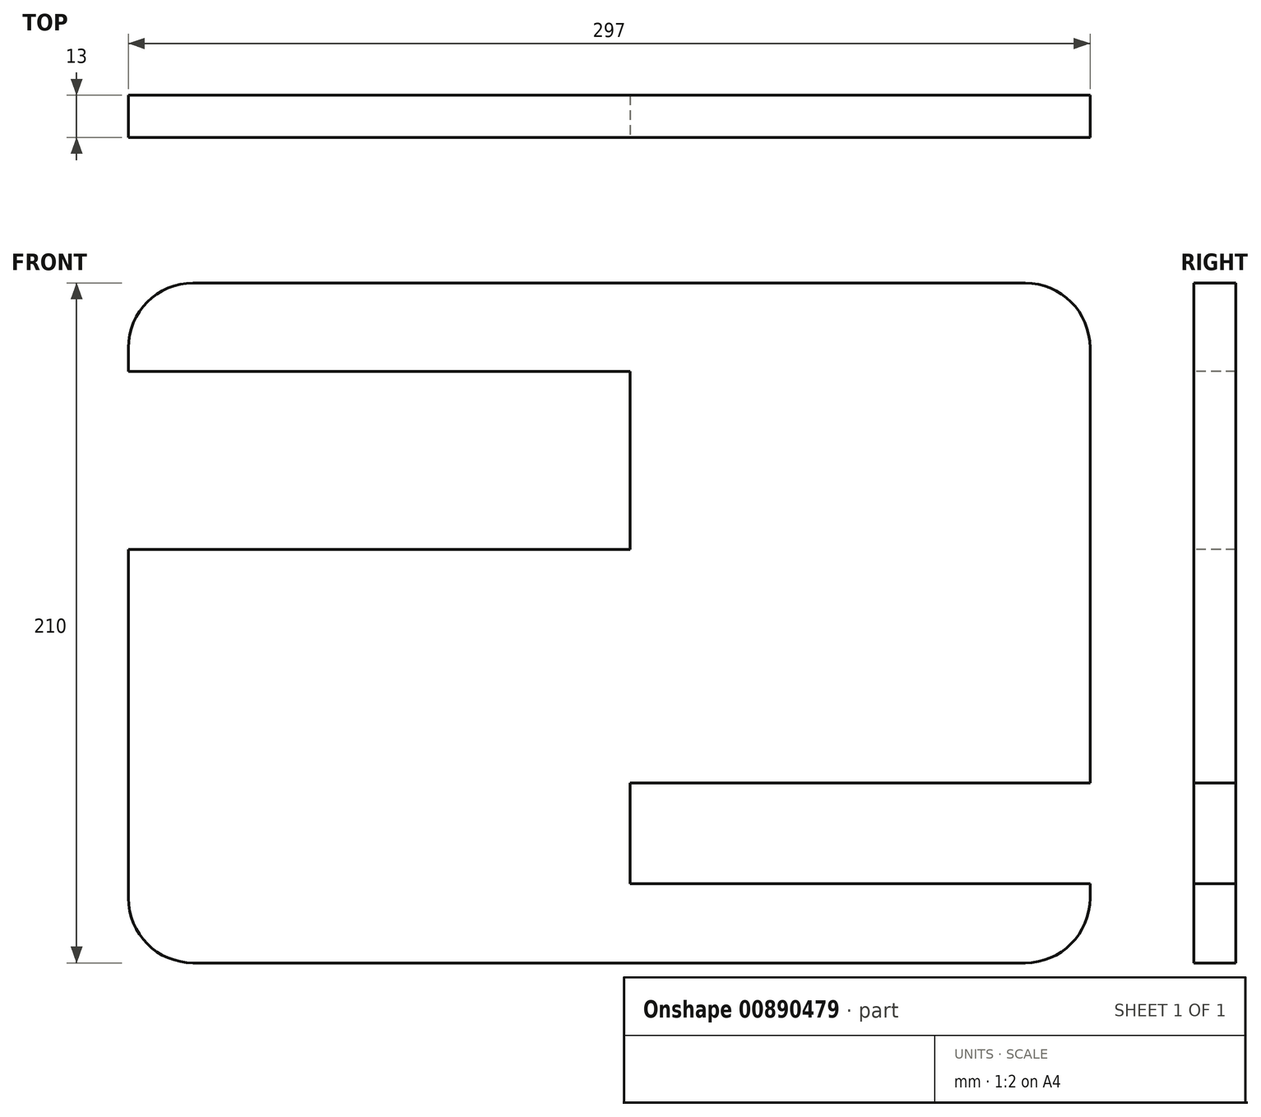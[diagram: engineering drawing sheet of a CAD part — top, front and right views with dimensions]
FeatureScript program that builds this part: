
annotation { "Feature Type Name" : "Feature", "Feature Type Description" : "" }
export const myFeature = defineFeature(function(context is Context, id is Id, definition is map)
    precondition{}
    {
        {
            var Q0;
            Q0=qCreatedBy(makeId("Front.planeOp"),FACE);
            var sketch = newSketch(context, id + "F0", { "sketchPlane" : qUnion([Q0])});
            skLineSegment(sketch, "E0.bottom", {"start": v(-107.63, 76.67) * mm, "end": v(149.37, 76.67) * mm});
            skLineSegment(sketch, "E0.top", {"start": v(-107.63, -133.33) * mm, "end": v(149.37, -133.33) * mm});
            skLineSegment(sketch, "E0.left", {"start": v(-127.63, 56.67) * mm, "end": v(-127.63, -113.33) * mm});
            skLineSegment(sketch, "E0.right", {"start": v(169.37, 56.67) * mm, "end": v(169.37, -113.33) * mm});
            skPoint(sketch, "E1.visualSharp", {"position": v(-127.63, 76.67) * mm});
            skArc(sketch, "E1.filletArc", {"start": v(-107.63, 76.67) * mm, "mid": v(-121.78, 70.81) * mm, "end": v(-127.63, 56.67) * mm});
            skPoint(sketch, "E2.visualSharp", {"position": v(169.37, 76.67) * mm});
            skArc(sketch, "E2.filletArc", {"start": v(169.37, 56.67) * mm, "mid": v(163.5, 70.81) * mm, "end": v(149.37, 76.67) * mm});
            skPoint(sketch, "E3.visualSharp", {"position": v(169.37, -133.33) * mm});
            skArc(sketch, "E3.filletArc", {"start": v(149.37, -133.33) * mm, "mid": v(163.5, -127.47) * mm, "end": v(169.37, -113.33) * mm});
            skPoint(sketch, "E4.visualSharp", {"position": v(-127.63, -133.33) * mm});
            skArc(sketch, "E4.filletArc", {"start": v(-127.63, -113.33) * mm, "mid": v(-121.78, -127.47) * mm, "end": v(-107.63, -133.33) * mm});
            skSolve(sketch);
        }
        {
            var Q0;
            Q0 = qSketchRegion(id + "F0", true);
            extrude(context, id + "F1", {"entities" : qUnion([Q0]), "depth" : 13 * mm, "offsetDistance" : 25 * mm});
        }
        {
            var Q0;
            Q0=makeQuery(id+"F1.opExtrude","CAP_FACE",FACE,{"disambiguationData":[OSD([sQuery(id+"F0.wireOp",EDGE,"E0.bottom"),sQuery(id+"F0.wireOp",EDGE,"E0.top"),sQuery(id+"F0.wireOp",EDGE,"E0.left"),sQuery(id+"F0.wireOp",EDGE,"E0.right"),sQuery(id+"F0.wireOp",EDGE,"E1.filletArc"),sQuery(id+"F0.wireOp",EDGE,"E2.filletArc"),sQuery(id+"F0.wireOp",EDGE,"E3.filletArc"),sQuery(id+"F0.wireOp",EDGE,"E4.filletArc")])],"isStart":false});
            var sketch = newSketch(context, id + "F2", { "sketchPlane" : qUnion([Q0])});
            skLineSegment(sketch, "E5.bottom", {"start": v(-127.63, 49.39) * mm, "end": v(27.37, 49.39) * mm});
            skLineSegment(sketch, "E5.top", {"start": v(-127.63, -5.61) * mm, "end": v(27.37, -5.61) * mm});
            skLineSegment(sketch, "E5.left", {"start": v(-127.63, 49.39) * mm, "end": v(-127.63, -5.61) * mm});
            skLineSegment(sketch, "E5.right", {"start": v(27.37, 49.39) * mm, "end": v(27.37, -5.61) * mm});
            skLineSegment(sketch, "E6.bottom", {"start": v(169.37, -77.82) * mm, "end": v(27.37, -77.82) * mm});
            skLineSegment(sketch, "E6.top", {"start": v(169.37, -108.82) * mm, "end": v(27.37, -108.82) * mm});
            skLineSegment(sketch, "E6.left", {"start": v(169.37, -77.82) * mm, "end": v(169.37, -108.82) * mm});
            skLineSegment(sketch, "E6.right", {"start": v(27.37, -77.82) * mm, "end": v(27.37, -108.82) * mm});
            skSolve(sketch);
        }
        {
            var Q0;
            Q0=makeQuery(id+"F2.imprint","IMPRINT",FACE,{"disambiguationData":[TD([[makeQuery(id+"F2.imprint","IMPRINT",EDGE,{"derivedFrom":sQuery(id+"F2.wireOp",EDGE,"E6.bottom")}),1.0]])]});
            var Q1;
            Q1=makeQuery(id+"F2.imprint","IMPRINT",FACE,{"disambiguationData":[TD([[makeQuery(id+"F2.imprint","IMPRINT",EDGE,{"derivedFrom":sQuery(id+"F2.wireOp",EDGE,"E5.bottom")}),-1.0]])]});
            extrude(context, id + "F3", {"entities" : qUnion([Q0, Q1]), "operationType" : NewBodyOperationType.REMOVE, "oppositeDirection" : true, "depth" : 25 * mm, "offsetDistance" : 25 * mm});
        }
    });
